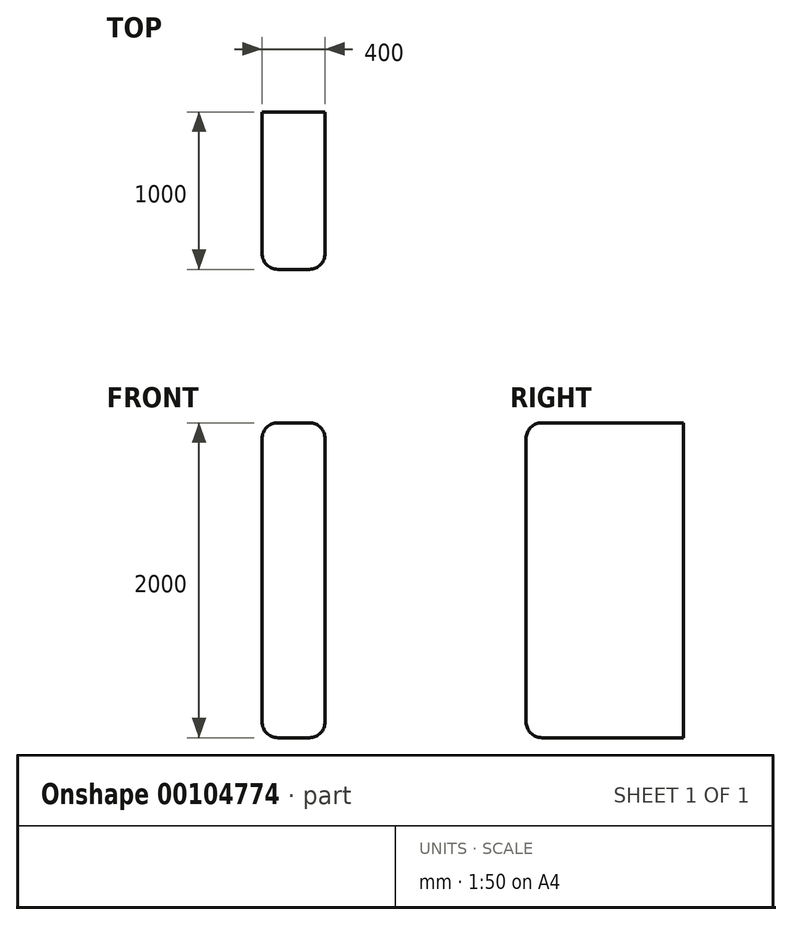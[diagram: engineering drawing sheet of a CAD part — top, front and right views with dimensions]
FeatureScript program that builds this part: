
annotation { "Feature Type Name" : "Feature", "Feature Type Description" : "" }
export const myFeature = defineFeature(function(context is Context, id is Id, definition is map)
    precondition{}
    {
        {
            var Q0;
            Q0=qCreatedBy(makeId("Right.planeOp"),FACE);
            var sketch = newSketch(context, id + "F0", { "sketchPlane" : qUnion([Q0])});
            skLineSegment(sketch, "E0.bottom", {"start": v(0, 0) * mm, "end": v(-1000, 0) * mm});
            skLineSegment(sketch, "E0.top", {"start": v(0, 2000) * mm, "end": v(-1000, 2000) * mm});
            skLineSegment(sketch, "E0.left", {"start": v(0, 0) * mm, "end": v(0, 2000) * mm});
            skLineSegment(sketch, "E0.right", {"start": v(-1000, 0) * mm, "end": v(-1000, 2000) * mm});
            skSolve(sketch);
        }
        {
            var Q0;
            Q0=makeQuery(id+"F0.imprint","IMPRINT",FACE,{"disambiguationData":[TD([[makeQuery(id+"F0.imprint","IMPRINT",EDGE,{"derivedFrom":sQuery(id+"F0.wireOp",EDGE,"E0.bottom")}),-1.0]])]});
            extrude(context, id + "F1", {"entities" : qUnion([Q0]), "depth" : 400 * mm});
        }
        {
            var Q0;
            Q0=makeQuery(id+"F1.opExtrude","CAP_EDGE",EDGE,{"disambiguationData":[OSD([sQuery(id+"F0.wireOp",EDGE,"E0.right")])],"isStart":true});
            var Q1;
            Q1=makeQuery(id+"F1.opExtrude","CAP_EDGE",EDGE,{"disambiguationData":[OSD([sQuery(id+"F0.wireOp",EDGE,"E0.right")])],"isStart":false});
            fillet(context, id + "F2", {"entities" : qUnion([Q0, Q1]), "radius" : 100 * mm, "tangentPropagation" : true, "allowEdgeOverflow" : false});
        }
        {
            var Q0;
            Q0=makeQuery(id+"F1.opExtrude","CAP_EDGE",EDGE,{"disambiguationData":[OSD([sQuery(id+"F0.wireOp",EDGE,"E0.bottom")])],"isStart":false});
            var Q1;
            Q1=makeQuery(id+"F2.opFillet","BLEND_EDGE",EDGE,{"blendedFrom":[makeQuery(id+"F1.opExtrude","CAP_EDGE",EDGE,{"disambiguationData":[OSD([sQuery(id+"F0.wireOp",EDGE,"E0.right")])],"isStart":false}),makeQuery(id+"F1.opExtrude","SWEPT_FACE",FACE,{"disambiguationData":[OSD([sQuery(id+"F0.wireOp",EDGE,"E0.bottom")])]})],"blendedInto":[makeQuery(id+"F1.opExtrude","SWEPT_FACE",FACE,{"disambiguationData":[OSD([sQuery(id+"F0.wireOp",EDGE,"E0.bottom")])]})]});
            var Q2;
            Q2=makeQuery(id+"F1.opExtrude","SWEPT_EDGE",EDGE,{"disambiguationData":[OSD([sQuery(id+"F0.wireOp",EDGE,"E0.bottom"),sQuery(id+"F0.wireOp",EDGE,"E0.right")])]});
            var Q3;
            Q3=makeQuery(id+"F2.opFillet","BLEND_EDGE",EDGE,{"blendedFrom":[makeQuery(id+"F1.opExtrude","CAP_EDGE",EDGE,{"disambiguationData":[OSD([sQuery(id+"F0.wireOp",EDGE,"E0.right")])],"isStart":true}),makeQuery(id+"F1.opExtrude","SWEPT_FACE",FACE,{"disambiguationData":[OSD([sQuery(id+"F0.wireOp",EDGE,"E0.bottom")])]})],"blendedInto":[makeQuery(id+"F1.opExtrude","SWEPT_FACE",FACE,{"disambiguationData":[OSD([sQuery(id+"F0.wireOp",EDGE,"E0.bottom")])]})]});
            var Q4;
            Q4=makeQuery(id+"F1.opExtrude","CAP_EDGE",EDGE,{"disambiguationData":[OSD([sQuery(id+"F0.wireOp",EDGE,"E0.bottom")])],"isStart":true});
            var Q5;
            Q5=makeQuery(id+"F1.opExtrude","CAP_EDGE",EDGE,{"disambiguationData":[OSD([sQuery(id+"F0.wireOp",EDGE,"E0.top")])],"isStart":false});
            var Q6;
            Q6=makeQuery(id+"F2.opFillet","BLEND_EDGE",EDGE,{"blendedFrom":[makeQuery(id+"F1.opExtrude","CAP_EDGE",EDGE,{"disambiguationData":[OSD([sQuery(id+"F0.wireOp",EDGE,"E0.right")])],"isStart":false}),makeQuery(id+"F1.opExtrude","SWEPT_FACE",FACE,{"disambiguationData":[OSD([sQuery(id+"F0.wireOp",EDGE,"E0.top")])]})],"blendedInto":[makeQuery(id+"F1.opExtrude","SWEPT_FACE",FACE,{"disambiguationData":[OSD([sQuery(id+"F0.wireOp",EDGE,"E0.top")])]})]});
            var Q7;
            Q7=makeQuery(id+"F1.opExtrude","SWEPT_EDGE",EDGE,{"disambiguationData":[OSD([sQuery(id+"F0.wireOp",EDGE,"E0.top"),sQuery(id+"F0.wireOp",EDGE,"E0.right")])]});
            var Q8;
            Q8=makeQuery(id+"F2.opFillet","BLEND_EDGE",EDGE,{"blendedFrom":[makeQuery(id+"F1.opExtrude","CAP_EDGE",EDGE,{"disambiguationData":[OSD([sQuery(id+"F0.wireOp",EDGE,"E0.right")])],"isStart":true}),makeQuery(id+"F1.opExtrude","SWEPT_FACE",FACE,{"disambiguationData":[OSD([sQuery(id+"F0.wireOp",EDGE,"E0.top")])]})],"blendedInto":[makeQuery(id+"F1.opExtrude","SWEPT_FACE",FACE,{"disambiguationData":[OSD([sQuery(id+"F0.wireOp",EDGE,"E0.top")])]})]});
            var Q9;
            Q9=makeQuery(id+"F1.opExtrude","CAP_EDGE",EDGE,{"disambiguationData":[OSD([sQuery(id+"F0.wireOp",EDGE,"E0.top")])],"isStart":true});
            fillet(context, id + "F3", {"entities" : qUnion([Q0, Q1, Q2, Q3, Q4, Q5, Q6, Q7, Q8, Q9]), "radius" : 100 * mm, "tangentPropagation" : true, "allowEdgeOverflow" : false});
        }
    });
